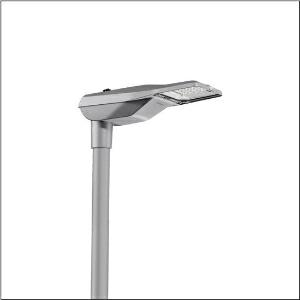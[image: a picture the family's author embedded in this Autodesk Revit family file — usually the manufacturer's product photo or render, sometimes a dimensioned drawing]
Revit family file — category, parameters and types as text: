
# Revit family: streetlight_sl_21_micro___st0_8a_5xe1c33s08db_f35f
name_source: partatom
category: Lighting Fixtures
units: mm (PartAtom-declared; Revit-internal decimal feet)

## family parameters
Cut with Voids When Loaded = No
Host = Face
Light Source = No
Part Type = Normal
Room Calculation Point = No
Round Connector Dimension = Use Diameter
Shared = No

## types (1)
- --- (1 x LED, 5110 lm, 39.1 W, 3000K)
    Apparent Load = 39 VA
    CIE Flux Codes = 38 75 97 100 100
    Color Rendering = 70
    Color Temperature = 3000K
    Default Elevation = 1800 mm
    Description = Streetlight SL 21 micro, mast luminaire, primary light control with lens, of PMMA, primary optical cover: cover, of toughened safety glass, transparent, light distribution: ST0.8a, light emission: direct distribution, primary light characteristic: asymmetric, installation type: side-entry, post-top, LED, High Power LED, rated luminous flux: 5.110lm, luminous efficacy: 131lm/W, light colour: 730, colour temperature: 3000K, control: flexible luminous flux parameterisation, time-dependent luminous flux control, constant luminous flux control, overheat protection, presetting dimming logarithmic, mains connection: 220..240V, AC, 50/60Hz, start of lifetime: 39W, end of service life: 41W, reduction: 18W, luminaire housing, of diecast aluminium, powder-coated, Siteco® metallic grey (DB 702S), corrosivity category C5 mid according to DIN EN ISO 12944, please order mast flange separately, inclination adjustable: 0°, 5°, 10°, 15°, sealing non-destructively replaceable, multi-level sealing system, length: 528mm, width: 235mm, height: 110mm, mast flange for spigot size: 42mm (side-entry): 5XC10008XM4, 60/48mm (side-entry/post-top): 5XC10108XM2, 76/60mm (side-entry/post-top): 5XC10108XM1, Smart Interface above, protection rating (complete): IP66, insulation class (complete): insulation class II (safety insulation), certification: CE, ENEC, ENEC+, VDE, impact resistance: IK09, permissible operating ambient temperature for outdoor applications: -40..+50°C, standard-compliant lighting for roads and squares, packaging unit: 1 piece

Light Distribution: ST0.8a
    Height = 110 mm
    Lamp = 1 x LED
    Lamp Light Flux = 5110 lm
    Lamp Power = 39.1 W
    Lamp count = 1
    Length = 528 mm
    Luminous efficacy = 131 lm/W
    Manufacturer = Siteco
    ModVariant = No
    Model = 5XE1C33S08DB
    Number of Poles = 1
    OnlyDefault = Yes
    Power Factor = 1
    Product Name = Streetlight SL 21 micro | ST0.8a
    Product group = mast luminaire | pylon top
    ProductGroupID = 6100
    Protection Class = Protection class II
    Protection Degree = IP 66
    RLX_Detail_Level = 1
    RLX_Emergency_Light_Flux = 0 lm
    RLX_Emergency_Type = 0
    RLX_Emergency_Type_DB = No
    RlxData = <blob elided: 98865 chars, md5=c365ac76>
    Socket = socket
    Standby Power = 0 W
    System Light Flux = 5110 lm
    System Power = 39 W
    Type Comments = factory setting: luminous flux: 100 % | dim-lin: 254 | 765 mA
    Type Image = l_1277292.jpg
    URL = http://relux.com
    VarID = @adj_104583
    Voltage = 0 V
    Weight = 0.00 kg
    Width = 235 mm

## geometry (parser evidence)
native form markers: Blend x4, Sweep x11
no freeform markers — native parametric forms only
